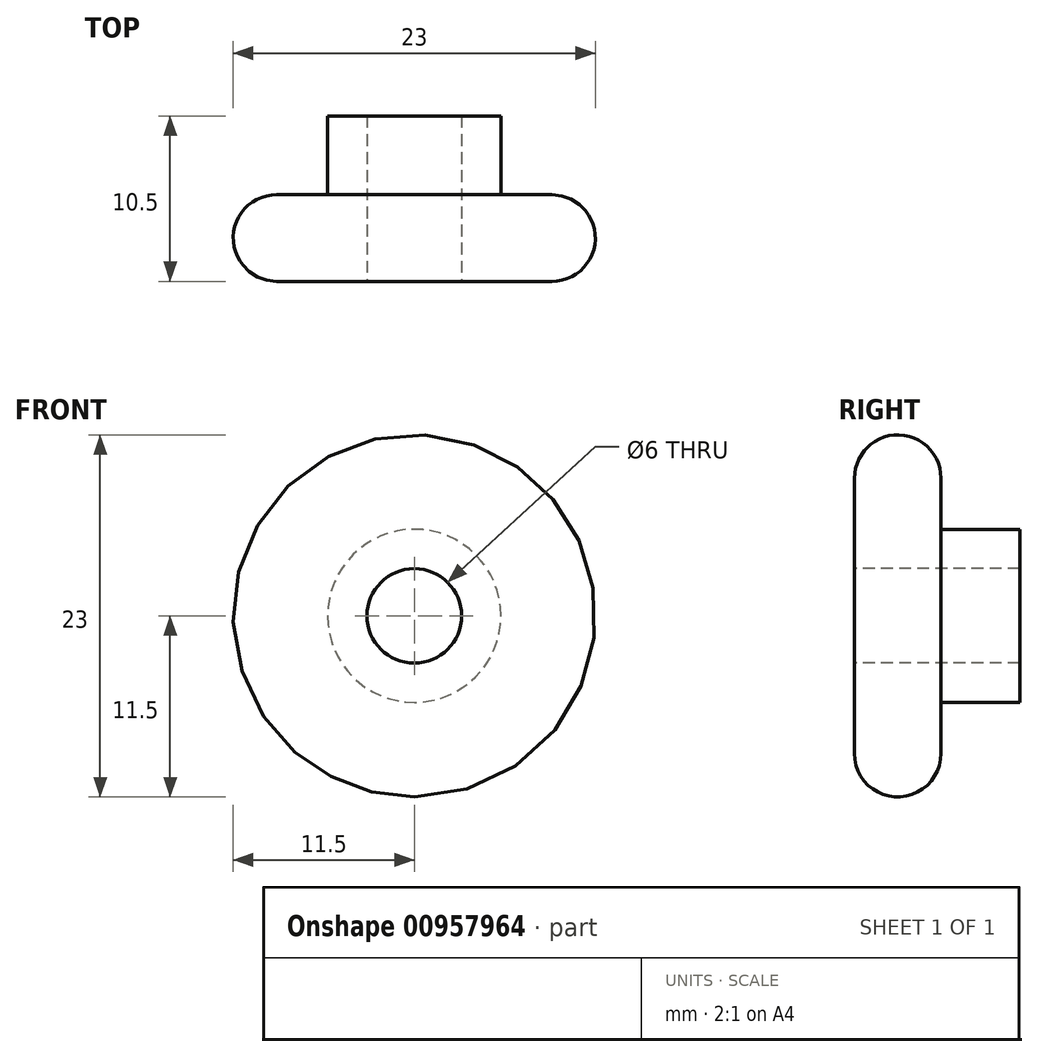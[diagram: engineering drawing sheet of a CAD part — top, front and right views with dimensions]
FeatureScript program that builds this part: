
annotation { "Feature Type Name" : "Feature", "Feature Type Description" : "" }
export const myFeature = defineFeature(function(context is Context, id is Id, definition is map)
    precondition{}
    {
        {
            var Q0;
            Q0=qCreatedBy(makeId("Top.planeOp"),FACE);
            var sketch = newSketch(context, id + "F0", { "sketchPlane" : qUnion([Q0])});
            skArc(sketch, "E0", {"start": v(8.75, -2.75) * mm, "mid": v(11.5, 0) * mm, "end": v(8.75, 2.75) * mm});
            skLineSegment(sketch, "E1", {"start": v(8.75, 2.75) * mm, "end": v(5.5, 2.75) * mm});
            skLineSegment(sketch, "E2", {"start": v(5.5, 2.75) * mm, "end": v(5.5, 7.75) * mm});
            skLineSegment(sketch, "E3", {"start": v(5.5, 7.75) * mm, "end": v(3, 7.75) * mm});
            skLineSegment(sketch, "E4", {"start": v(3, 7.75) * mm, "end": v(3, -2.75) * mm});
            skLineSegment(sketch, "E5", {"start": v(3, -2.75) * mm, "end": v(8.75, -2.75) * mm});
            skLineSegment(sketch, "E6", {"start": v(0, -7.74) * mm, "end": v(0, 13.64) * mm, "construction": true});
            skSolve(sketch);
        }
        {
            var Q0;
            Q0=makeQuery(id+"F0.imprint","IMPRINT",FACE,{"disambiguationData":[TD([[makeQuery(id+"F0.imprint","IMPRINT",EDGE,{"derivedFrom":sQuery(id+"F0.wireOp",EDGE,"E0")}),1.0]])]});
            var Q1;
            Q1=sQuery(id+"F0.wireOp",EDGE,"E6");
            revolve(context, id + "F1", {"surfaceOperationType" : NewSurfaceOperationType.NEW, "entities" : qUnion([Q0]), "axis" : qUnion([Q1]), "revolveType" : RevolveType.FULL});
        }
    });
